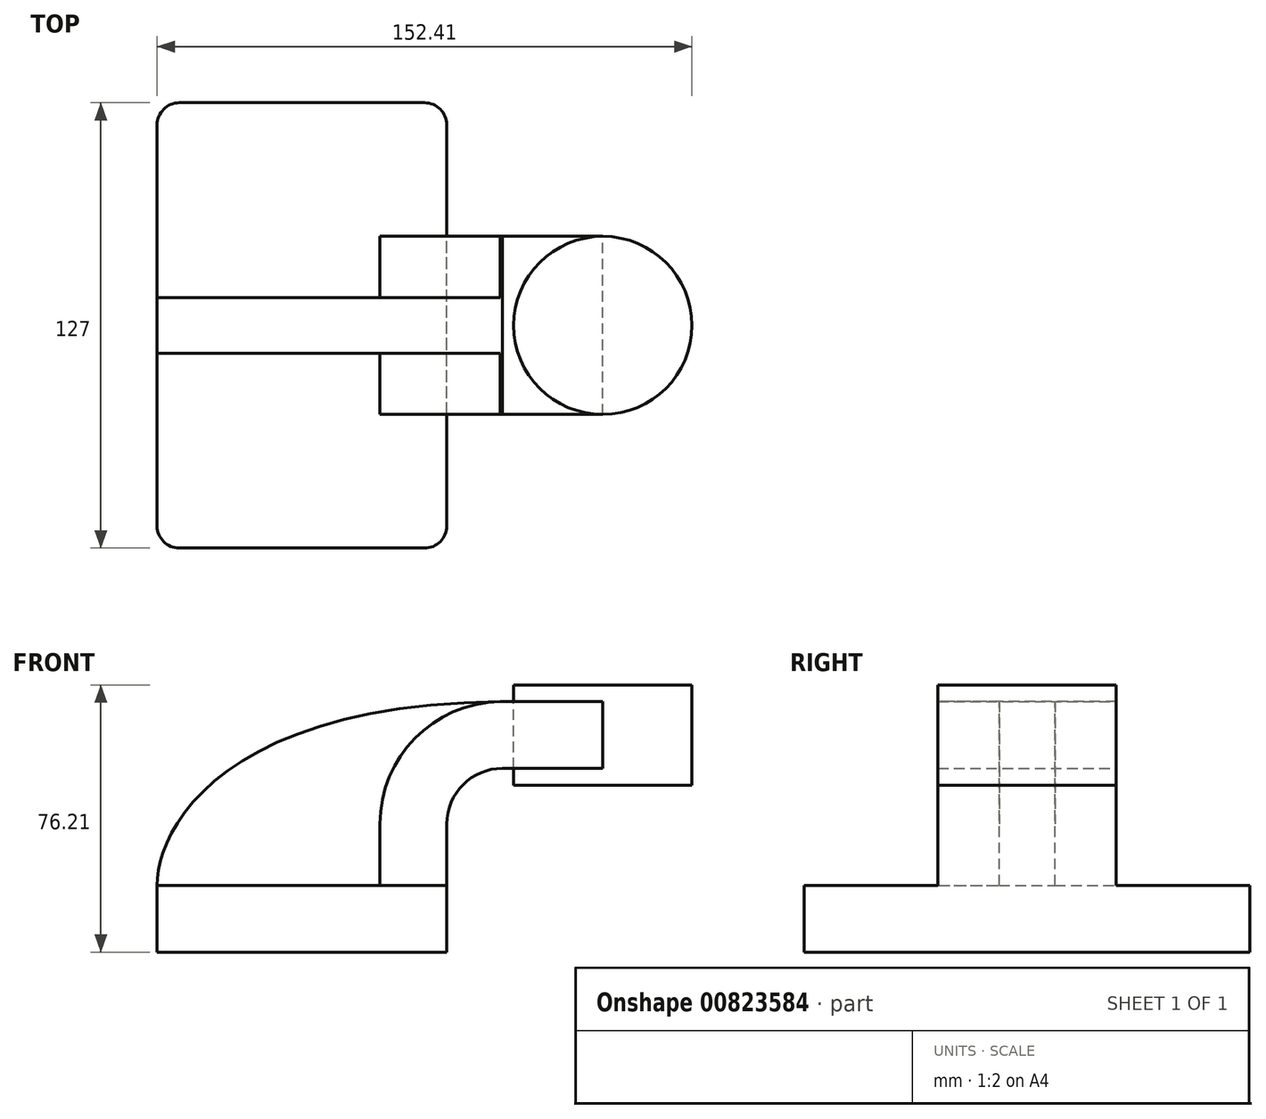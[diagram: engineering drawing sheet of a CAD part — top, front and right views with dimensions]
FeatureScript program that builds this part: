
annotation { "Feature Type Name" : "Feature", "Feature Type Description" : "" }
export const myFeature = defineFeature(function(context is Context, id is Id, definition is map)
    precondition{}
    {
        {
            var Q0;
            Q0=qCreatedBy(makeId("Front.planeOp"),FACE);
            var sketch = newSketch(context, id + "F0", { "sketchPlane" : qUnion([Q0])});
            skLineSegment(sketch, "E0.bottom", {"start": v(41.28, -9.52) * mm, "end": v(-41.27, -9.53) * mm});
            skLineSegment(sketch, "E0.top", {"start": v(41.27, 9.53) * mm, "end": v(-41.28, 9.53) * mm});
            skLineSegment(sketch, "E0.left", {"start": v(41.28, -9.52) * mm, "end": v(41.28, 9.53) * mm});
            skLineSegment(sketch, "E0.right", {"start": v(-41.27, -9.53) * mm, "end": v(-41.28, 9.53) * mm});
            skPoint(sketch, "E0.middle", {"position": v(0, 0) * mm});
            skLineSegment(sketch, "E1.bottom", {"start": v(111.12, 38.1) * mm, "end": v(60.32, 38.1) * mm});
            skLineSegment(sketch, "E1.top", {"start": v(111.12, 66.68) * mm, "end": v(60.32, 66.68) * mm});
            skLineSegment(sketch, "E1.left", {"start": v(111.12, 38.1) * mm, "end": v(111.12, 66.68) * mm});
            skLineSegment(sketch, "E1.right", {"start": v(60.32, 38.1) * mm, "end": v(60.32, 66.67) * mm});
            skPoint(sketch, "E1.middle", {"position": v(85.72, 52.39) * mm});
            skLineSegment(sketch, "E2", {"start": v(41.27, 9.53) * mm, "end": v(41.27, 27) * mm});
            skArc(sketch, "E3", {"start": v(41.27, 27) * mm, "mid": v(45.92, 38.23) * mm, "end": v(57.15, 42.88) * mm});
            skLineSegment(sketch, "E4", {"start": v(57.15, 42.88) * mm, "end": v(85.72, 42.88) * mm});
            skLineSegment(sketch, "E5.0", {"start": v(57.15, 61.93) * mm, "end": v(85.72, 61.93) * mm});
            skArc(sketch, "E5.1", {"start": v(22.23, 27) * mm, "mid": v(32.45, 51.7) * mm, "end": v(57.15, 61.93) * mm});
            skLineSegment(sketch, "E5.2", {"start": v(22.22, 9.53) * mm, "end": v(22.22, 27) * mm});
            skLineSegment(sketch, "E6", {"start": v(85.72, 61.93) * mm, "end": v(85.72, 42.88) * mm});
            skFitSpline(sketch, "E7", {"points": [v(-41.28, 9.52) * mm, v(57.15, 61.93) * mm], "startDerivative": vector(-0.83, 43.24) * mm, "endDerivative": vector(246.15, 2.16) * mm});
            skLineSegment(sketch, "E8", {"start": v(85.72, 66.68) * mm, "end": v(85.72, 38.1) * mm});
            skSolve(sketch);
        }
        {
            var Q0;
            Q0=makeQuery(id+"F0.imprint","IMPRINT",FACE,{"disambiguationData":[TD([[makeQuery(id+"F0.imprint","IMPRINT",EDGE,{"derivedFrom":sQuery(id+"F0.wireOp",EDGE,"E0.bottom")}),-1.0]])]});
            extrude(context, id + "F1", {"entities" : qUnion([Q0]), "endBound" : BoundingType.SYMMETRIC, "depth" : 127 * mm, "offsetDistance" : 25.4 * mm});
        }
        {
            var Q0;
            {var subQ1=sQuery(id+"F0.wireOp",EDGE,"E2");Q0=makeQuery(id+"F0.imprint","IMPRINT",FACE,{"disambiguationData":[TD([[makeQuery(id+"F0.imprint","IMPRINT",EDGE,{"derivedFrom":subQ1}),1.0]])]});}
            var Q1;
            {var subQ5=sQuery(id+"F0.wireOp",EDGE,"E6");Q1=makeQuery(id+"F0.imprint","IMPRINT",FACE,{"disambiguationData":[TD([[makeQuery(id+"F0.imprint","IMPRINT",EDGE,{"derivedFrom":subQ5}),-1.0]])]});}
            var Q2;
            {var subQ0=sQuery(id+"F0.wireOp",EDGE,"E4");var subQ1=sQuery(id+"F0.wireOp",EDGE,"E1.right");var subQ2=makeQuery(id+"F0.imprint","INTERSECT",VERTEX,{"derivedFrom":[subQ1,subQ0]});Q2=makeQuery(id+"F0.imprint","IMPRINT",FACE,{"disambiguationData":[TD([[makeQuery(id+"F0.imprint","IMPRINT",EDGE,{"disambiguationData":[TD([[subQ2,-1.0]])],"derivedFrom":subQ1}),-1.0]])]});}
            extrude(context, id + "F2", {"entities" : qUnion([Q0, Q1, Q2]), "operationType" : NewBodyOperationType.ADD, "endBound" : BoundingType.SYMMETRIC, "depth" : 50.8 * mm, "offsetDistance" : 25.4 * mm});
        }
        {
            var Q0;
            {var subQ3=sQuery(id+"F0.wireOp",EDGE,"E5.2");Q0=makeQuery(id+"F0.imprint","IMPRINT",FACE,{"disambiguationData":[TD([[makeQuery(id+"F0.imprint","IMPRINT",EDGE,{"derivedFrom":subQ3}),1.0]])]});}
            extrude(context, id + "F3", {"entities" : qUnion([Q0]), "operationType" : NewBodyOperationType.ADD, "endBound" : BoundingType.SYMMETRIC, "depth" : 15.88 * mm, "offsetDistance" : 25.4 * mm});
        }
        {
            var Q0;
            {var subQ4=sQuery(id+"F0.wireOp",EDGE,"E1.left");Q0=makeQuery(id+"F0.imprint","IMPRINT",FACE,{"disambiguationData":[TD([[makeQuery(id+"F0.imprint","IMPRINT",EDGE,{"derivedFrom":subQ4}),1.0]])]});}
            var Q1;
            Q1=sQuery(id+"F0.wireOp",EDGE,"E8");
            revolve(context, id + "F4", {"surfaceOperationType" : NewSurfaceOperationType.NEW, "entities" : qUnion([Q0]), "axis" : qUnion([Q1]), "revolveType" : RevolveType.FULL});
        }
        {
            var Q0;
            Q0=makeQuery(id+"F1.opExtrude","CAP_EDGE",EDGE,{"disambiguationData":[OSD([sQuery(id+"F0.wireOp",EDGE,"E0.left")])],"isStart":false});
            var Q1;
            Q1=makeQuery(id+"F1.opExtrude","CAP_EDGE",EDGE,{"disambiguationData":[OSD([sQuery(id+"F0.wireOp",EDGE,"E0.right")])],"isStart":false});
            var Q2;
            Q2=makeQuery(id+"F1.opExtrude","CAP_EDGE",EDGE,{"disambiguationData":[OSD([sQuery(id+"F0.wireOp",EDGE,"E0.right")])],"isStart":true});
            var Q3;
            Q3=makeQuery(id+"F1.opExtrude","CAP_EDGE",EDGE,{"disambiguationData":[OSD([sQuery(id+"F0.wireOp",EDGE,"E0.left")])],"isStart":true});
            fillet(context, id + "F5", {"entities" : qUnion([Q0, Q1, Q2, Q3]), "radius" : 6.35 * mm, "tangentPropagation" : true, "allowEdgeOverflow" : false});
        }
    });
